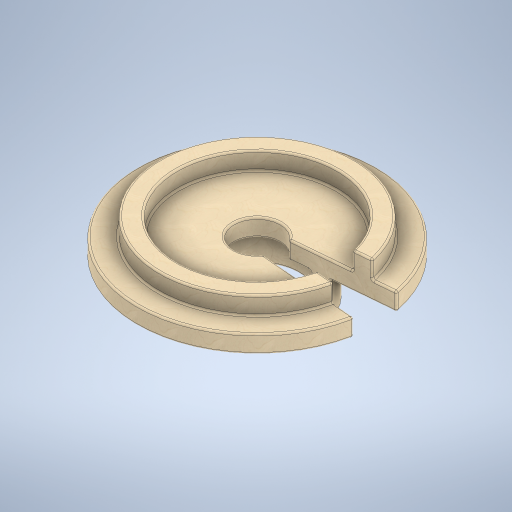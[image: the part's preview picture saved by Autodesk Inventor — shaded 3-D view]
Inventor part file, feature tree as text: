
AUTODESK INVENTOR PART (.ipt)
format: ipt  version: 2024 (Build 280153000, 153)  size: 559,616 bytes
history: native  units: in
note: dims shown in document units (in); Inventor stores cm internally (conversion verified against a paired STEP export)
features: fillet x2, sketch x2, revolve x1, direct_edit x1, extrude x1, other x1, projected_geometry x1
ambient origin geometry x8: Origin, YZ Plane, XZ Plane, XY Plane, X Axis, Y Axis, Z Axis, Center Point
bodies: Solid1 (feature_tree)
feature tree (9):
  revolve  "Revolution1"  [1 undecoded]
  direct_edit  "Direct Edit1"
  extrude  "Extrusion1"  Depth=0.05in
  fillet  "Fillet1"  Radius=0.05in
  fillet  "Fillet2"  Radius=0.1in
  sketch  "Sketch1"  dims[d0=0.05in d1=0.13in]
  sketch  "Sketch2"  dims[d2=0.45in d3=0.05in d4=0.05in d5=0.1in d6=0.675in d7=0.235in d8=0.1in d9=90.0deg d10=3.937in d11=0.3937in d12=0.3937in d13=0.625in d14=0.0687in d15=0.0in d16=0.0in d17=0.05in d18=0.05in]
  other  "Scale1"
  projected_geometry  "Project Cut Edges1"
note: 1 required parameter value undecoded (feature->parameter linkage not recoverable at this tier; creation-order binding heuristic only, values carry confidence <= 0.55)
